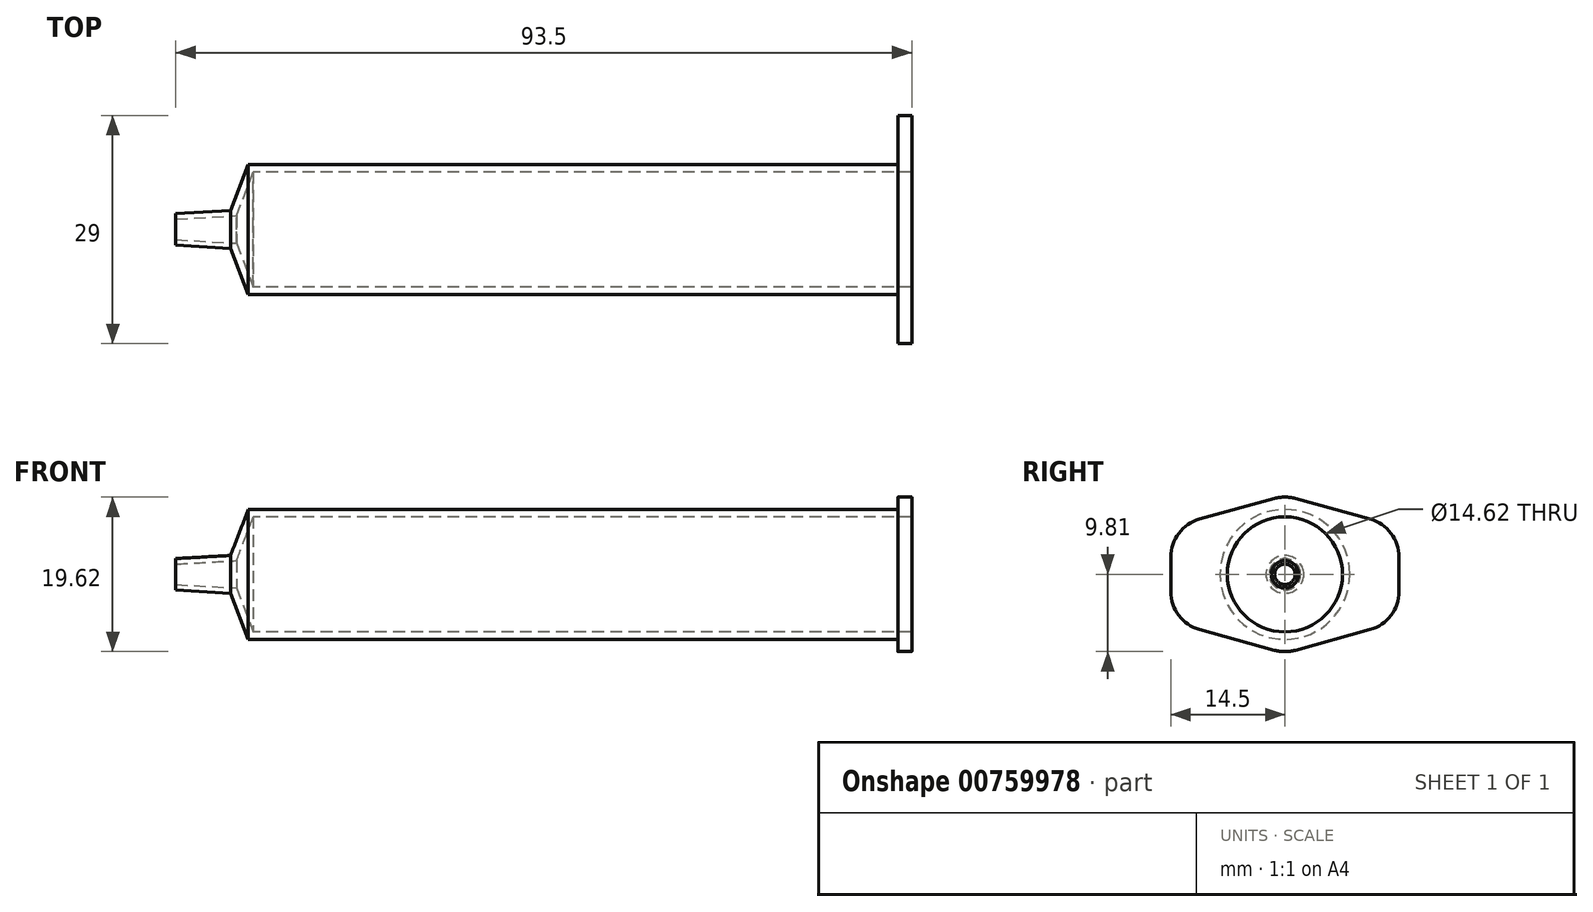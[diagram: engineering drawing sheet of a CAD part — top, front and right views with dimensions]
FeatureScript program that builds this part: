
annotation { "Feature Type Name" : "Feature", "Feature Type Description" : "" }
export const myFeature = defineFeature(function(context is Context, id is Id, definition is map)
    precondition{}
    {
        {
            var Q0;
            Q0=qCreatedBy(makeId("Top.planeOp"),FACE);
            var sketch = newSketch(context, id + "F0", { "sketchPlane" : qUnion([Q0])});
            skLineSegment(sketch, "E0", {"start": v(9.2, 8.25) * mm, "end": v(91.7, 8.25) * mm});
            skLineSegment(sketch, "E1", {"start": v(91.7, 8.25) * mm, "end": v(91.7, 7.3) * mm});
            skLineSegment(sketch, "E2", {"start": v(91.7, 7.3) * mm, "end": v(9.85, 7.3) * mm});
            skLineSegment(sketch, "E3", {"start": v(9.85, 7.31) * mm, "end": v(7.7, 1.74) * mm});
            skLineSegment(sketch, "E4", {"start": v(0, 1.3) * mm, "end": v(0, 2) * mm});
            skLineSegment(sketch, "E5", {"start": v(0, 2) * mm, "end": v(6.95, 2.4) * mm});
            skLineSegment(sketch, "E6.trimOffspring", {"start": v(6.95, 2.4) * mm, "end": v(9.2, 8.25) * mm});
            skLineSegment(sketch, "E7", {"start": v(0, 1.3) * mm, "end": v(7.7, 1.74) * mm});
            skLineSegment(sketch, "E8", {"start": v(0, 0) * mm, "end": v(81.03, 0) * mm});
            skSolve(sketch);
        }
        {
            var Q0;
            Q0=makeQuery(id+"F0.imprint","IMPRINT",FACE,{"disambiguationData":[TD([[makeQuery(id+"F0.imprint","IMPRINT",EDGE,{"derivedFrom":sQuery(id+"F0.wireOp",EDGE,"E0")}),-1.0]])]});
            var Q1;
            Q1=sQuery(id+"F0.wireOp",EDGE,"E8");
            revolve(context, id + "F1", {"surfaceOperationType" : NewSurfaceOperationType.NEW, "entities" : qUnion([Q0]), "axis" : qUnion([Q1]), "revolveType" : RevolveType.FULL});
        }
        {
            var Q0;
            Q0=makeQuery(id+"F1.opRevolve","SWEPT_FACE",FACE,{"disambiguationData":[OSD([sQuery(id+"F0.wireOp",EDGE,"E1")])]});
            var sketch = newSketch(context, id + "F2", { "sketchPlane" : qUnion([Q0])});
            skCircle(sketch, "E9.0", {"center": v(0, 0) * mm, "radius": 7.31 * mm});
            skLineSegment(sketch, "E10", {"start": v(-14.5, 0) * mm, "end": v(-14.5, 6) * mm});
            skLineSegment(sketch, "E11", {"start": v(-14.5, 6) * mm, "end": v(0, 10) * mm});
            skLineSegment(sketch, "E12", {"start": v(0, 10) * mm, "end": v(14.5, 6) * mm});
            skLineSegment(sketch, "E13", {"start": v(14.5, 6) * mm, "end": v(14.5, 0) * mm});
            skLineSegment(sketch, "E14.MirrorCS", {"start": v(14.5, -6) * mm, "end": v(14.5, 0) * mm});
            skLineSegment(sketch, "E15.MirrorCS", {"start": v(0, -10) * mm, "end": v(14.5, -6) * mm});
            skLineSegment(sketch, "E16.MirrorCS", {"start": v(-14.5, 0) * mm, "end": v(-14.5, -6) * mm});
            skLineSegment(sketch, "E17.MirrorCS", {"start": v(-14.5, -6) * mm, "end": v(0, -10) * mm});
            skSolve(sketch);
        }
        {
            var Q0;
            Q0 = qSketchRegion(id + "F2", true);
            extrude(context, id + "F3", {"entities" : qUnion([Q0]), "operationType" : NewBodyOperationType.ADD, "depth" : 1.8 * mm, "offsetDistance" : 25 * mm});
        }
        {
            var Q0;
            Q0=makeQuery(id+"F3.opExtrude","SWEPT_EDGE",EDGE,{"disambiguationData":[OSD([sQuery(id+"F2.wireOp",EDGE,"E10"),sQuery(id+"F2.wireOp",EDGE,"E11")])]});
            var Q1;
            Q1=makeQuery(id+"F3.opExtrude","SWEPT_EDGE",EDGE,{"disambiguationData":[OSD([sQuery(id+"F2.wireOp",EDGE,"E16.MirrorCS"),sQuery(id+"F2.wireOp",EDGE,"E17.MirrorCS")])]});
            var Q2;
            Q2=makeQuery(id+"F3.opExtrude","SWEPT_EDGE",EDGE,{"disambiguationData":[OSD([sQuery(id+"F2.wireOp",EDGE,"E15.MirrorCS"),sQuery(id+"F2.wireOp",EDGE,"E17.MirrorCS")])]});
            var Q3;
            Q3=makeQuery(id+"F3.opExtrude","SWEPT_EDGE",EDGE,{"disambiguationData":[OSD([sQuery(id+"F2.wireOp",EDGE,"E14.MirrorCS"),sQuery(id+"F2.wireOp",EDGE,"E15.MirrorCS")])]});
            var Q4;
            Q4=makeQuery(id+"F3.opExtrude","SWEPT_EDGE",EDGE,{"disambiguationData":[OSD([sQuery(id+"F2.wireOp",EDGE,"E12"),sQuery(id+"F2.wireOp",EDGE,"E13")])]});
            var Q5;
            Q5=makeQuery(id+"F3.opExtrude","SWEPT_EDGE",EDGE,{"disambiguationData":[OSD([sQuery(id+"F2.wireOp",EDGE,"E11"),sQuery(id+"F2.wireOp",EDGE,"E12")])]});
            fillet(context, id + "F4", {"entities" : qUnion([Q0, Q1, Q2, Q3, Q4, Q5]), "radius" : 5 * mm, "tangentPropagation" : true, "allowEdgeOverflow" : false});
        }
    });
